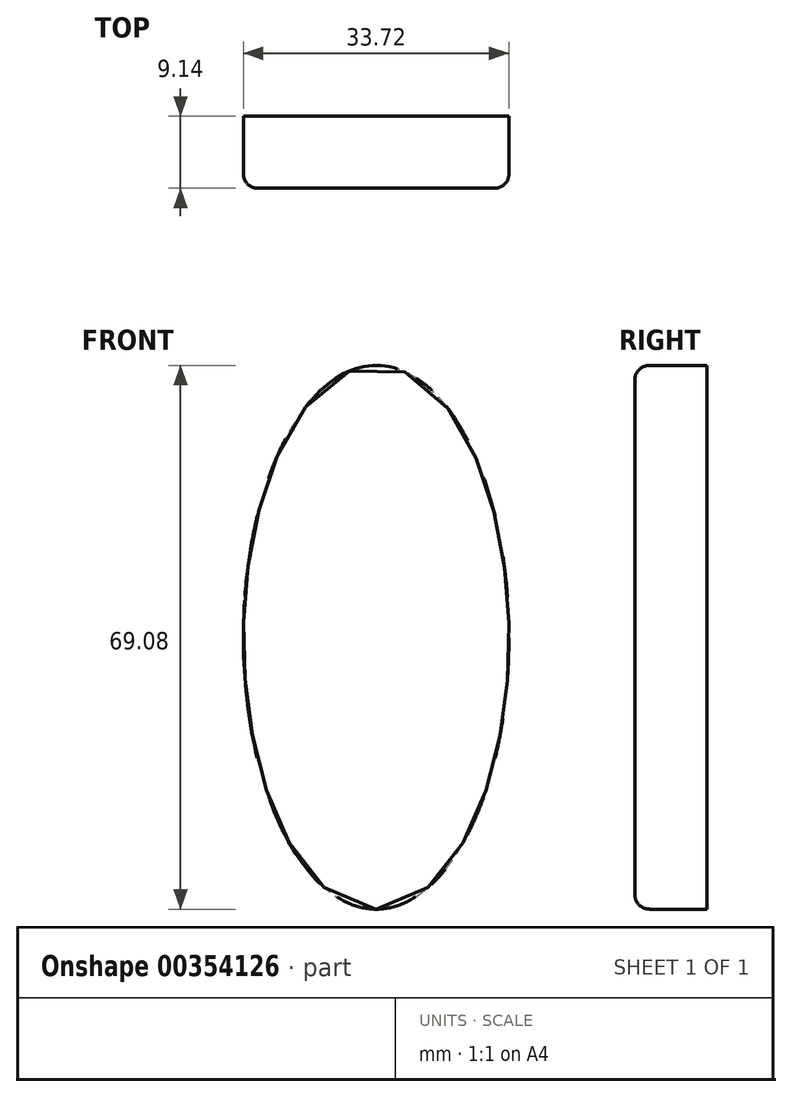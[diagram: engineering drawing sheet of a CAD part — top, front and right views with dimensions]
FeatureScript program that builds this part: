
annotation { "Feature Type Name" : "Feature", "Feature Type Description" : "" }
export const myFeature = defineFeature(function(context is Context, id is Id, definition is map)
    precondition{}
    {
        {
            var Q0;
            Q0=qCreatedBy(makeId("Front.planeOp"),FACE);
            var sketch = newSketch(context, id + "F0", { "sketchPlane" : qUnion([Q0])});
            skEllipse(sketch, "E0", {"center": v(-31.95, 18.42) * mm, "majorRadius": 34.54 * mm, "minorRadius": 16.86 * mm, "majorAxis": v(0, -1)});
            skSolve(sketch);
        }
        {
            var Q0;
            Q0=makeQuery(id+"F0.imprint","IMPRINT",FACE,{"disambiguationData":[TD([[makeQuery(id+"F0.imprint","IMPRINT",EDGE,{"derivedFrom":sQuery(id+"F0.wireOp",EDGE,"E0")}),1.0]])]});
            extrude(context, id + "F1", {"entities" : qUnion([Q0]), "depth" : 9.14 * mm});
        }
        {
            var Q0;
            Q0=makeQuery(id+"F1.opExtrude","CAP_FACE",FACE,{"disambiguationData":[OSD([sQuery(id+"F0.wireOp",EDGE,"E0")])],"isStart":false});
            fillet(context, id + "F2", {"entities" : qUnion([Q0]), "radius" : 1.84 * mm, "tangentPropagation" : true, "allowEdgeOverflow" : false});
        }
    });
